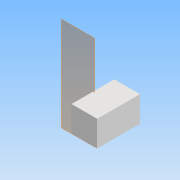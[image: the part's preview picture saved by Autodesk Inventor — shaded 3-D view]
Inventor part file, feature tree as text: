
AUTODESK INVENTOR PART (.ipt)
format: ipt  version: 2021 (Build 250183000, 183)  size: 84,992 bytes
history: native  units: mm
features: other x4, plane x1, extrude x1, sketch x1
ambient origin geometry x8: Origin, YZ Plane, XZ Plane, XY Plane, X Axis, Y Axis, Z Axis, Center Point
bodies: Body1 (feature_tree)
feature tree (7):
  other  "實體1"
  plane  "工作平面1"
  extrude  "擠出1"  Depth=600.0mm
  sketch  "草圖1"
  other  "參考1"
  other  "組合1"
  other  "車身:1"
